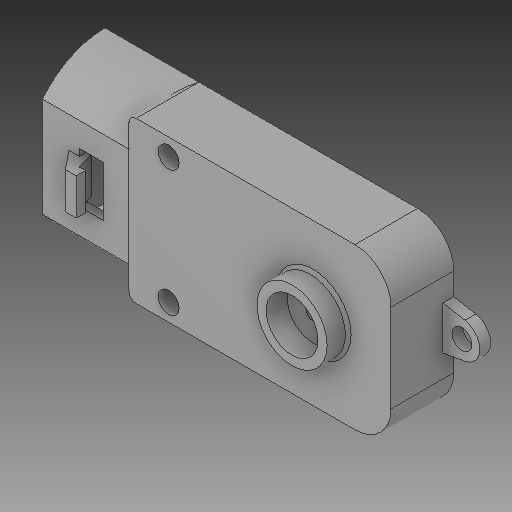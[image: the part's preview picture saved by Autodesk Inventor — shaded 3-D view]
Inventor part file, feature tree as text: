
AUTODESK INVENTOR PART (.ipt)
format: ipt  version: 2019 (Build 230136000, 136)  size: 166,400 bytes
history: mixed  units: mm
features: chamfer x1, imported_body x1
ambient origin geometry x8: Origin, YZ Plane, XZ Plane, XY Plane, X Axis, Y Axis, Z Axis, Center Point
bodies: Solid1 (imported_parasolid)
feature tree (2):
  chamfer  "Chamfer1"  [1 undecoded]
  imported_body  NMx_Import_Brep_tag  [imported B-rep: ~31 faces, bbox_mm=[43.3235, 22.225, 11.23696]]
note: 1 required parameter value undecoded (feature->parameter linkage not recoverable at this tier; creation-order binding heuristic only, values carry confidence <= 0.55)
